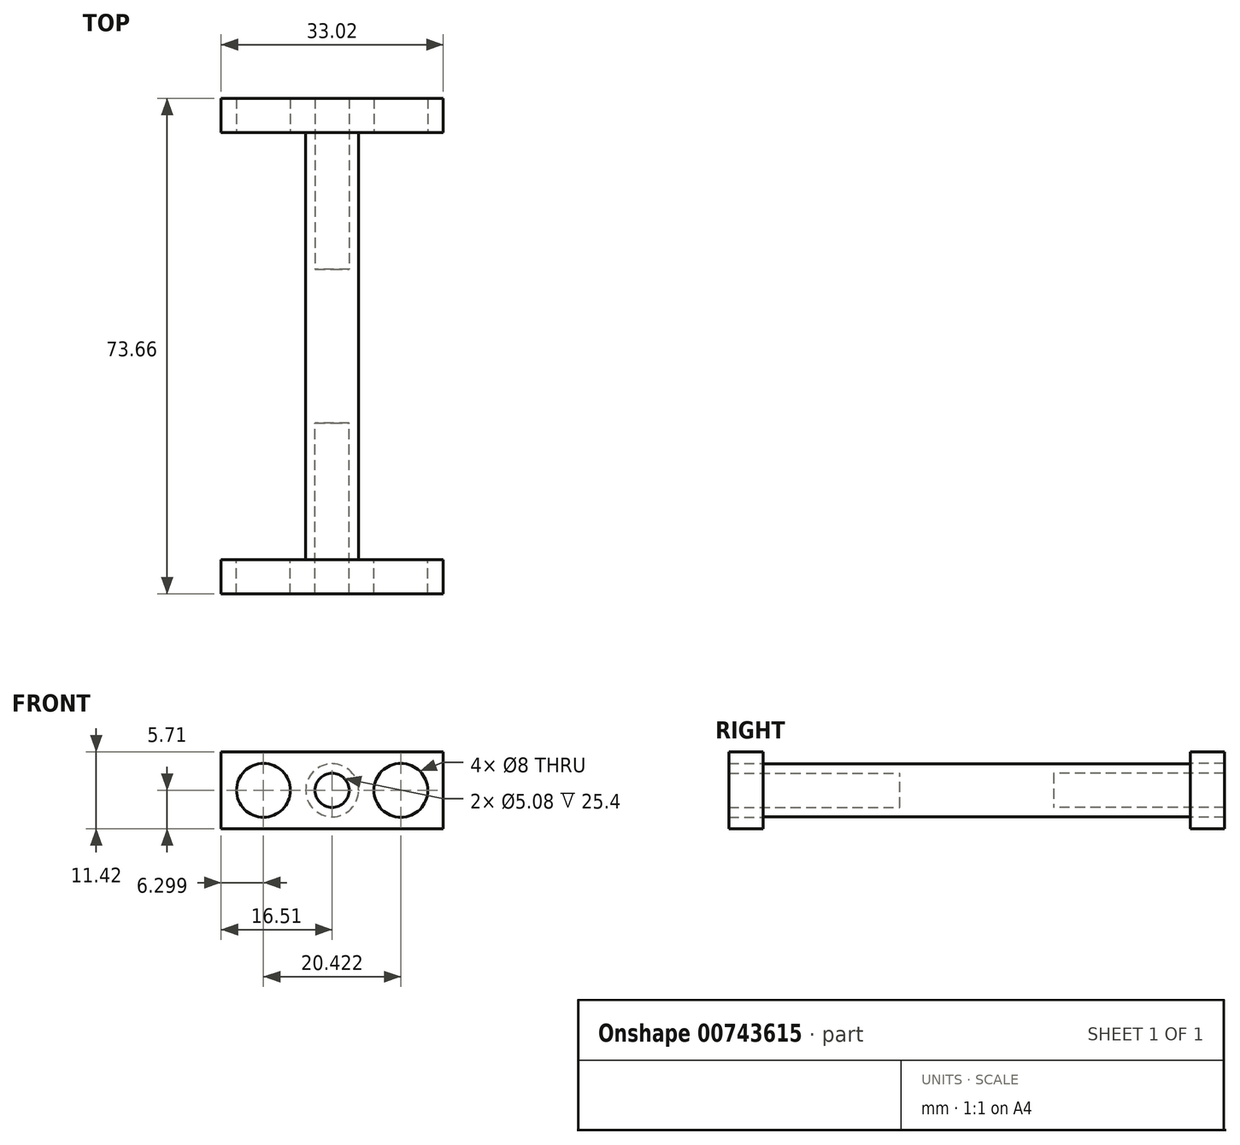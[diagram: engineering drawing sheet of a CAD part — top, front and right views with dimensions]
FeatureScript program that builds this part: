
annotation { "Feature Type Name" : "Feature", "Feature Type Description" : "" }
export const myFeature = defineFeature(function(context is Context, id is Id, definition is map)
    precondition{}
    {
        {
            var Q0;
            Q0=qCreatedBy(makeId("Front.planeOp"),FACE);
            var sketch = newSketch(context, id + "F0", { "sketchPlane" : qUnion([Q0])});
            skCircle(sketch, "E0", {"center": v(0, 0) * mm, "radius": 3.94 * mm});
            skSolve(sketch);
        }
        {
            var Q0;
            Q0 = qSketchRegion(id + "F0", true);
            extrude(context, id + "F1", {"entities" : qUnion([Q0]), "depth" : 63.5 * mm, "offsetDistance" : 25.4 * mm});
        }
        {
            var Q0;
            Q0=makeQuery(id+"F1.opExtrude","CAP_FACE",FACE,{"disambiguationData":[OSD([sQuery(id+"F0.wireOp",EDGE,"E0")])],"isStart":false});
            var sketch = newSketch(context, id + "F2", { "sketchPlane" : qUnion([Q0])});
            skLineSegment(sketch, "E1.bottom", {"start": v(-16.51, 5.72) * mm, "end": v(16.51, 5.72) * mm});
            skLineSegment(sketch, "E1.top", {"start": v(-16.51, -5.72) * mm, "end": v(16.51, -5.72) * mm});
            skLineSegment(sketch, "E1.left", {"start": v(-16.51, 5.72) * mm, "end": v(-16.51, -5.71) * mm});
            skLineSegment(sketch, "E1.right", {"start": v(16.51, 5.72) * mm, "end": v(16.51, -5.71) * mm});
            skPoint(sketch, "E1.middle", {"position": v(0, 0) * mm});
            skCircle(sketch, "E2", {"center": v(-10.21, 0) * mm, "radius": 4 * mm});
            skLineSegment(sketch, "E3", {"start": v(0, 5.72) * mm, "end": v(0, -5.72) * mm, "construction": true});
            skCircle(sketch, "E4.MirrorC", {"center": v(10.21, 0) * mm, "radius": 4 * mm});
            skCircle(sketch, "E5", {"center": v(0, 0) * mm, "radius": 2.54 * mm});
            skSolve(sketch);
        }
        {
            var Q0;
            Q0 = qSketchRegion(id + "F2", true);
            extrude(context, id + "F3", {"entities" : qUnion([Q0]), "operationType" : NewBodyOperationType.ADD, "depth" : 5.08 * mm, "offsetDistance" : 25.4 * mm});
        }
        {
            var Q0;
            Q0=makeQuery(id+"F1.opExtrude","CAP_FACE",FACE,{"disambiguationData":[OSD([sQuery(id+"F0.wireOp",EDGE,"E0")])],"isStart":false});
            extrude(context, id + "F4", {"entities" : qUnion([Q0]), "operationType" : NewBodyOperationType.REMOVE, "oppositeDirection" : true, "depth" : 20.32 * mm, "offsetDistance" : 25.4 * mm});
        }
        {
            var Q0;
            Q0=makeQuery(id+"F1.opExtrude","CAP_FACE",FACE,{"disambiguationData":[OSD([sQuery(id+"F0.wireOp",EDGE,"E0")])],"isStart":true});
            var sketch = newSketch(context, id + "F5", { "sketchPlane" : qUnion([Q0])});
            skLineSegment(sketch, "E6.bottom", {"start": v(-16.51, 5.71) * mm, "end": v(16.51, 5.71) * mm});
            skLineSegment(sketch, "E6.top", {"start": v(-16.51, -5.71) * mm, "end": v(16.51, -5.71) * mm});
            skLineSegment(sketch, "E6.left", {"start": v(-16.51, 5.71) * mm, "end": v(-16.51, -5.71) * mm});
            skLineSegment(sketch, "E6.right", {"start": v(16.51, 5.71) * mm, "end": v(16.51, -5.71) * mm});
            skPoint(sketch, "E6.middle", {"position": v(0, 0) * mm});
            skCircle(sketch, "E7", {"center": v(0, 0) * mm, "radius": 2.54 * mm});
            skCircle(sketch, "E8", {"center": v(-10.21, 0) * mm, "radius": 4 * mm});
            skLineSegment(sketch, "E9", {"start": v(0, 5.71) * mm, "end": v(0, -5.71) * mm, "construction": true});
            skCircle(sketch, "E10.MirrorC", {"center": v(10.21, 0) * mm, "radius": 4 * mm});
            skSolve(sketch);
        }
        {
            var Q0;
            Q0 = qSketchRegion(id + "F5", true);
            extrude(context, id + "F6", {"entities" : qUnion([Q0]), "operationType" : NewBodyOperationType.ADD, "depth" : 5.08 * mm, "offsetDistance" : 25.4 * mm});
        }
        {
            var Q0;
            Q0=makeQuery(id+"F1.opExtrude","CAP_FACE",FACE,{"disambiguationData":[OSD([sQuery(id+"F0.wireOp",EDGE,"E0")])],"isStart":true});
            extrude(context, id + "F7", {"entities" : qUnion([Q0]), "operationType" : NewBodyOperationType.REMOVE, "oppositeDirection" : true, "depth" : 20.32 * mm, "offsetDistance" : 25.4 * mm});
        }
    });
